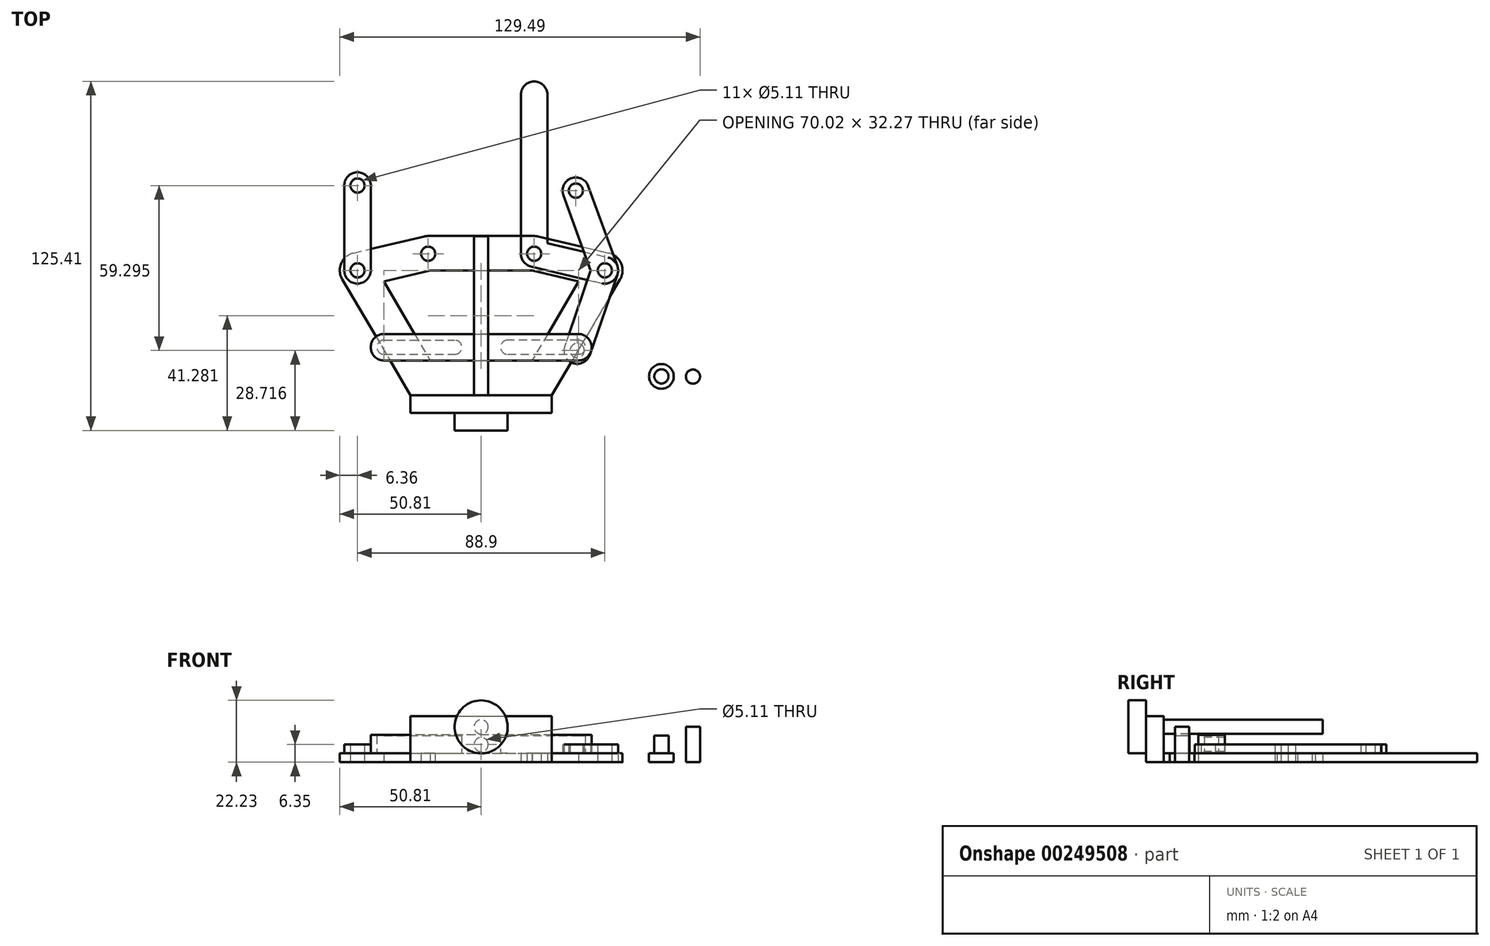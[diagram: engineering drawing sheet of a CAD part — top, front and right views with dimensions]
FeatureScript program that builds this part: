
annotation { "Feature Type Name" : "Feature", "Feature Type Description" : "" }
export const myFeature = defineFeature(function(context is Context, id is Id, definition is map)
    precondition{}
    {
        {
            var Q0;
            Q0=qCreatedBy(makeId("Top.planeOp"),FACE);
            var sketch = newSketch(context, id + "F0", { "sketchPlane" : qUnion([Q0])});
            skLineSegment(sketch, "E0", {"start": v(0, 0) * mm, "end": v(0, 50.8) * mm, "construction": true});
            skLineSegment(sketch, "E1", {"start": v(-44.45, 44.83) * mm, "end": v(44.45, 44.83) * mm, "construction": true});
            skLineSegment(sketch, "E2", {"start": v(-19.05, 50.8) * mm, "end": v(19.05, 50.8) * mm, "construction": true});
            skPoint(sketch, "E3", {"position": v(0, 44.83) * mm});
            skCircle(sketch, "E4", {"center": v(-19.05, 50.8) * mm, "radius": 2.55 * mm});
            skCircle(sketch, "E5", {"center": v(19.05, 50.8) * mm, "radius": 2.55 * mm});
            skCircle(sketch, "E6", {"center": v(44.45, 44.83) * mm, "radius": 2.55 * mm});
            skCircle(sketch, "E7", {"center": v(-44.45, 44.83) * mm, "radius": 2.55 * mm});
            skArc(sketch, "E8.0", {"start": v(20.5, 57) * mm, "mid": v(19.78, 57.12) * mm, "end": v(19.05, 57.16) * mm});
            skArc(sketch, "E9.0", {"start": v(49.93, 41.6) * mm, "mid": v(50.3, 47.33) * mm, "end": v(45.9, 51.02) * mm});
            skArc(sketch, "E10.0", {"start": v(-19.05, 57.16) * mm, "mid": v(-19.78, 57.12) * mm, "end": v(-20.5, 57) * mm});
            skArc(sketch, "E11.0", {"start": v(-45.9, 51.02) * mm, "mid": v(-50.3, 47.33) * mm, "end": v(-49.93, 41.6) * mm});
            skLineSegment(sketch, "E12", {"start": v(-25.4, 0) * mm, "end": v(25.4, 0) * mm});
            skLineSegment(sketch, "E13", {"start": v(-45.9, 51.02) * mm, "end": v(-20.5, 57) * mm});
            skLineSegment(sketch, "E14", {"start": v(-49.93, 41.6) * mm, "end": v(-25.4, 0) * mm});
            skLineSegment(sketch, "E15", {"start": v(-19.05, 57.16) * mm, "end": v(19.05, 57.16) * mm});
            skLineSegment(sketch, "E16", {"start": v(20.5, 57) * mm, "end": v(45.9, 51.02) * mm});
            skLineSegment(sketch, "E17", {"start": v(49.93, 41.6) * mm, "end": v(25.4, 0) * mm});
            skPoint(sketch, "E18", {"position": v(0, 0) * mm});
            skLineSegment(sketch, "E19.0", {"start": v(-35.01, 40.8) * mm, "end": v(-18.34, 44.72) * mm});
            skLineSegment(sketch, "E19.1", {"start": v(18.34, 44.72) * mm, "end": v(35.01, 40.8) * mm});
            skLineSegment(sketch, "E19.2", {"start": v(35.01, 40.8) * mm, "end": v(18.3, 12.45) * mm});
            skLineSegment(sketch, "E19.3", {"start": v(-18.34, 44.72) * mm, "end": v(18.34, 44.72) * mm});
            skLineSegment(sketch, "E19.4", {"start": v(-18.3, 12.45) * mm, "end": v(18.3, 12.45) * mm});
            skLineSegment(sketch, "E19.5", {"start": v(-35.01, 40.8) * mm, "end": v(-18.3, 12.45) * mm});
            skSolve(sketch);
        }
        {
            var Q0;
            Q0 = qSketchRegion(id + "F0", true);
            extrude(context, id + "F1", {"entities" : qUnion([Q0]), "depth" : 3.17 * mm});
        }
        {
            var Q0;
            Q0=makeQuery(id+"F1.opExtrude","CAP_FACE",FACE,{"disambiguationData":[OSD([sQuery(id+"F0.wireOp",EDGE,"E4"),sQuery(id+"F0.wireOp",EDGE,"E5"),sQuery(id+"F0.wireOp",EDGE,"E6"),sQuery(id+"F0.wireOp",EDGE,"E7"),sQuery(id+"F0.wireOp",EDGE,"E8.0"),sQuery(id+"F0.wireOp",EDGE,"E9.0"),sQuery(id+"F0.wireOp",EDGE,"E10.0"),sQuery(id+"F0.wireOp",EDGE,"E11.0"),sQuery(id+"F0.wireOp",EDGE,"E12"),sQuery(id+"F0.wireOp",EDGE,"E13"),sQuery(id+"F0.wireOp",EDGE,"E14"),sQuery(id+"F0.wireOp",EDGE,"E15"),sQuery(id+"F0.wireOp",EDGE,"E16"),sQuery(id+"F0.wireOp",EDGE,"E17"),sQuery(id+"F0.wireOp",EDGE,"E19.0"),sQuery(id+"F0.wireOp",EDGE,"E19.1"),sQuery(id+"F0.wireOp",EDGE,"E19.2"),sQuery(id+"F0.wireOp",EDGE,"E19.3"),sQuery(id+"F0.wireOp",EDGE,"E19.4"),sQuery(id+"F0.wireOp",EDGE,"E19.5")])],"isStart":false});
            var sketch = newSketch(context, id + "F2", { "sketchPlane" : qUnion([Q0])});
            skCircle(sketch, "E20.0", {"center": v(-44.45, 44.83) * mm, "radius": 2.55 * mm});
            skCircle(sketch, "E21", {"center": v(-44.45, 44.83) * mm, "radius": 4.76 * mm});
            skLineSegment(sketch, "E22", {"start": v(-44.45, 44.83) * mm, "end": v(-44.45, 75.31) * mm, "construction": true});
            skCircle(sketch, "E23", {"center": v(-44.45, 75.31) * mm, "radius": 4.76 * mm});
            skCircle(sketch, "E24", {"center": v(-44.45, 75.31) * mm, "radius": 2.55 * mm});
            skLineSegment(sketch, "E25", {"start": v(-49.21, 75.31) * mm, "end": v(-49.21, 44.83) * mm});
            skLineSegment(sketch, "E26", {"start": v(-39.69, 75.31) * mm, "end": v(-39.69, 44.83) * mm});
            skSolve(sketch);
        }
        {
            var Q0;
            Q0 = qSketchRegion(id + "F2", true);
            extrude(context, id + "F3", {"entities" : qUnion([Q0]), "depth" : 3.17 * mm});
        }
        {
            var Q0;
            Q0=makeQuery(id+"F2.imprint","IMPRINT",FACE,{"disambiguationData":[TD([[makeQuery(id+"F2.imprint","IMPRINT",EDGE,{"derivedFrom":makeQuery(id+"F1.opExtrude","CAP_EDGE",EDGE,{"disambiguationData":[OSD([sQuery(id+"F0.wireOp",EDGE,"E4")])],"isStart":false})}),-1.0]])]});
            var sketch = newSketch(context, id + "F4", { "sketchPlane" : qUnion([Q0])});
            skLineSegment(sketch, "E27.bottom", {"start": v(34.93, 21.97) * mm, "end": v(-34.93, 21.97) * mm});
            skLineSegment(sketch, "E27.top", {"start": v(34.93, 12.45) * mm, "end": v(-34.93, 12.45) * mm});
            skLineSegment(sketch, "E27.left", {"start": v(34.93, 21.97) * mm, "end": v(34.93, 19.76) * mm});
            skLineSegment(sketch, "E27.right", {"start": v(-34.93, 21.97) * mm, "end": v(-34.93, 19.76) * mm});
            skPoint(sketch, "E27.middle", {"position": v(0, 17.2) * mm});
            skArc(sketch, "E28", {"start": v(34.93, 12.45) * mm, "mid": v(39.69, 17.2) * mm, "end": v(34.93, 21.97) * mm});
            skArc(sketch, "E29", {"start": v(-34.93, 21.97) * mm, "mid": v(-39.69, 17.2) * mm, "end": v(-34.93, 12.45) * mm});
            skCircle(sketch, "E30.0", {"center": v(-44.45, 44.83) * mm, "radius": 2.55 * mm, "construction": true});
            skPoint(sketch, "E31.0", {"position": v(-18.3, 12.45) * mm});
            skPoint(sketch, "E32.0", {"position": v(-25.4, 0) * mm});
            skPoint(sketch, "E33.0", {"position": v(18.3, 12.45) * mm});
            skPoint(sketch, "E34.0", {"position": v(25.4, 0) * mm});
            skLineSegment(sketch, "E35", {"start": v(-18.3, 12.45) * mm, "end": v(-25.4, 0) * mm, "construction": true});
            skLineSegment(sketch, "E36", {"start": v(18.3, 12.45) * mm, "end": v(25.4, 0) * mm, "construction": true});
            skLineSegment(sketch, "E37.0", {"start": v(-18.3, 12.45) * mm, "end": v(18.3, 12.45) * mm, "construction": true});
            skArc(sketch, "E38", {"start": v(34.93, 14.66) * mm, "mid": v(37.48, 17.2) * mm, "end": v(34.93, 19.76) * mm});
            skArc(sketch, "E39", {"start": v(-34.93, 19.76) * mm, "mid": v(-37.48, 17.2) * mm, "end": v(-34.93, 14.66) * mm});
            skArc(sketch, "E40", {"start": v(-9.53, 14.66) * mm, "mid": v(-6.97, 17.2) * mm, "end": v(-9.53, 19.76) * mm});
            skArc(sketch, "E41", {"start": v(9.53, 19.76) * mm, "mid": v(6.97, 17.2) * mm, "end": v(9.53, 14.66) * mm});
            skLineSegment(sketch, "E42", {"start": v(-34.93, 19.76) * mm, "end": v(-9.53, 19.76) * mm});
            skLineSegment(sketch, "E43", {"start": v(-34.93, 14.66) * mm, "end": v(-9.53, 14.66) * mm});
            skLineSegment(sketch, "E44", {"start": v(9.53, 14.66) * mm, "end": v(34.93, 14.66) * mm});
            skLineSegment(sketch, "E45", {"start": v(34.93, 19.76) * mm, "end": v(9.53, 19.76) * mm});
            skLineSegment(sketch, "E46", {"start": v(-34.93, 17.2) * mm, "end": v(-9.53, 17.2) * mm, "construction": true});
            skLineSegment(sketch, "E47", {"start": v(9.53, 17.2) * mm, "end": v(34.93, 17.2) * mm, "construction": true});
            skLineSegment(sketch, "E48.trimOffspring", {"start": v(34.93, 14.66) * mm, "end": v(34.93, 12.45) * mm});
            skLineSegment(sketch, "E49.trimOffspring", {"start": v(-34.93, 14.66) * mm, "end": v(-34.93, 12.45) * mm});
            skSolve(sketch);
        }
        {
            var Q0;
            Q0 = qSketchRegion(id + "F4", true);
            extrude(context, id + "F5", {"entities" : qUnion([Q0]), "depth" : 6.35 * mm});
        }
        {
            var Q0;
            Q0=makeQuery(id+"F2.imprint","IMPRINT",FACE,{"disambiguationData":[TD([[makeQuery(id+"F2.imprint","IMPRINT",EDGE,{"derivedFrom":makeQuery(id+"F1.opExtrude","CAP_EDGE",EDGE,{"disambiguationData":[OSD([sQuery(id+"F0.wireOp",EDGE,"E4")])],"isStart":false})}),-1.0]])]});
            var sketch = newSketch(context, id + "F6", { "sketchPlane" : qUnion([Q0])});
            skCircle(sketch, "E50.0", {"center": v(44.45, 44.83) * mm, "radius": 2.55 * mm});
            skArc(sketch, "E51", {"start": v(48.95, 43.28) * mm, "mid": v(49.21, 44.87) * mm, "end": v(48.93, 46.46) * mm});
            skArc(sketch, "E52", {"start": v(38.5, 75.1) * mm, "mid": v(32.4, 77.95) * mm, "end": v(29.55, 71.84) * mm});
            skLineSegment(sketch, "E53", {"start": v(34.03, 73.47) * mm, "end": v(44.45, 44.83) * mm, "construction": true});
            skLineSegment(sketch, "E54", {"start": v(38.5, 75.1) * mm, "end": v(48.93, 46.46) * mm});
            skLineSegment(sketch, "E55", {"start": v(29.55, 71.84) * mm, "end": v(39.4, 44.79) * mm});
            skCircle(sketch, "E56", {"center": v(34.03, 73.47) * mm, "radius": 2.55 * mm});
            skCircle(sketch, "E57.0", {"center": v(34.51, 16.02) * mm, "radius": 2.55 * mm});
            skCircle(sketch, "E58", {"center": v(34.51, 16.02) * mm, "radius": 4.76 * mm});
            skLineSegment(sketch, "E59", {"start": v(39.4, 44.79) * mm, "end": v(30.01, 17.57) * mm});
            skLineSegment(sketch, "E60", {"start": v(48.95, 43.28) * mm, "end": v(39.02, 14.46) * mm});
            skSolve(sketch);
        }
        {
            var Q0;
            Q0 = qSketchRegion(id + "F6", true);
            extrude(context, id + "F7", {"entities" : qUnion([Q0]), "depth" : 3.17 * mm});
        }
        {
            var Q0;
            Q0=qCreatedBy(makeId("Top.planeOp"),FACE);
            var sketch = newSketch(context, id + "F8", { "sketchPlane" : qUnion([Q0])});
            skCircle(sketch, "E61", {"center": v(64.8, 6.73) * mm, "radius": 4.45 * mm});
            skSolve(sketch);
        }
        {
            var Q0;
            Q0 = qSketchRegion(id + "F8", true);
            extrude(context, id + "F9", {"entities" : qUnion([Q0]), "depth" : 3.17 * mm});
        }
        {
            var Q0;
            Q0=makeQuery(id+"F9.opExtrude","CAP_FACE",FACE,{"disambiguationData":[OSD([sQuery(id+"F8.wireOp",EDGE,"E61")])],"isStart":false});
            var sketch = newSketch(context, id + "F10", { "sketchPlane" : qUnion([Q0])});
            skCircle(sketch, "E62", {"center": v(64.8, 6.73) * mm, "radius": 2.55 * mm});
            skSolve(sketch);
        }
        {
            var Q0;
            Q0 = qSketchRegion(id + "F10", true);
            extrude(context, id + "F11", {"entities" : qUnion([Q0]), "operationType" : NewBodyOperationType.ADD, "depth" : 6.35 * mm});
        }
        {
            var Q0;
            Q0=qCreatedBy(makeId("Top.planeOp"),FACE);
            var sketch = newSketch(context, id + "F12", { "sketchPlane" : qUnion([Q0])});
            skCircle(sketch, "E63.0", {"center": v(19.05, 50.8) * mm, "radius": 2.55 * mm});
            skCircle(sketch, "E64.0", {"center": v(44.45, 44.83) * mm, "radius": 2.55 * mm});
            skCircle(sketch, "E65", {"center": v(19.05, 50.8) * mm, "radius": 4.76 * mm});
            skCircle(sketch, "E66", {"center": v(44.45, 44.83) * mm, "radius": 4.76 * mm});
            skLineSegment(sketch, "E67", {"start": v(20.14, 55.44) * mm, "end": v(45.54, 49.47) * mm});
            skLineSegment(sketch, "E68", {"start": v(17.96, 46.16) * mm, "end": v(43.36, 40.2) * mm});
            skCircle(sketch, "E69", {"center": v(19.05, 107.95) * mm, "radius": 4.76 * mm});
            skLineSegment(sketch, "E70", {"start": v(14.29, 107.95) * mm, "end": v(14.29, 50.8) * mm});
            skLineSegment(sketch, "E71", {"start": v(23.81, 50.8) * mm, "end": v(23.81, 107.95) * mm});
            skSolve(sketch);
        }
        {
            var Q0;
            Q0 = qSketchRegion(id + "F12", true);
            extrude(context, id + "F13", {"entities" : qUnion([Q0]), "depth" : 3.17 * mm});
        }
        {
            var Q0;
            Q0=qCreatedBy(makeId("Top.planeOp"),FACE);
            var sketch = newSketch(context, id + "F14", { "sketchPlane" : qUnion([Q0])});
            skCircle(sketch, "E72", {"center": v(76.12, 6.64) * mm, "radius": 2.55 * mm});
            skSolve(sketch);
        }
        {
            var Q0;
            Q0 = qSketchRegion(id + "F14", true);
            extrude(context, id + "F15", {"entities" : qUnion([Q0]), "depth" : 12.7 * mm});
        }
        {
            var Q0;
            Q0=makeQuery(id+"F5.opExtrude","CAP_FACE",FACE,{"disambiguationData":[OSD([sQuery(id+"F4.wireOp",EDGE,"E27.bottom"),sQuery(id+"F4.wireOp",EDGE,"E27.top"),sQuery(id+"F4.wireOp",EDGE,"E28"),sQuery(id+"F4.wireOp",EDGE,"E29"),sQuery(id+"F4.wireOp",EDGE,"E38"),sQuery(id+"F4.wireOp",EDGE,"E39"),sQuery(id+"F4.wireOp",EDGE,"E40"),sQuery(id+"F4.wireOp",EDGE,"E41"),sQuery(id+"F4.wireOp",EDGE,"E42"),sQuery(id+"F4.wireOp",EDGE,"E43"),sQuery(id+"F4.wireOp",EDGE,"E44"),sQuery(id+"F4.wireOp",EDGE,"E45")])],"isStart":false});
            var sketch = newSketch(context, id + "F16", { "sketchPlane" : qUnion([Q0])});
            skLineSegment(sketch, "E73.0", {"start": v(34.93, 21.97) * mm, "end": v(34.93, 21.97) * mm});
            skLineSegment(sketch, "E74.0", {"start": v(34.93, 21.97) * mm, "end": v(-34.93, 21.97) * mm});
            skArc(sketch, "E75.0", {"start": v(34.93, 12.45) * mm, "mid": v(39.69, 17.2) * mm, "end": v(34.93, 21.97) * mm});
            skLineSegment(sketch, "E76.0", {"start": v(34.93, 12.45) * mm, "end": v(-34.93, 12.45) * mm});
            skArc(sketch, "E77.0", {"start": v(-34.93, 21.97) * mm, "mid": v(-39.69, 17.2) * mm, "end": v(-34.93, 12.45) * mm});
            skSolve(sketch);
        }
        {
            var Q0;
            Q0 = qSketchRegion(id + "F16", true);
            extrude(context, id + "F17", {"entities" : qUnion([Q0]), "operationType" : NewBodyOperationType.ADD, "depth" : 0.25 * mm});
        }
        {
            var Q0;
            Q0=makeQuery(id+"F17.boolean.opBoolean","MERGE",FACE,{"derivedFrom":[makeQuery(id+"F5.opExtrude","SWEPT_FACE",FACE,{"disambiguationData":[OSD([sQuery(id+"F4.wireOp",EDGE,"E27.top")])]}),makeQuery(id+"F17.opExtrude","SWEPT_FACE",FACE,{"disambiguationData":[OSD([sQuery(id+"F16.wireOp",EDGE,"890eed87-c472-4494-b1f9-d9110c023a10.0")])]})]});
            var sketch = newSketch(context, id + "F18", { "sketchPlane" : qUnion([Q0])});
            skCircle(sketch, "E78", {"center": v(0, 6.35) * mm, "radius": 2.55 * mm});
            skSolve(sketch);
        }
        {
            var Q0;
            Q0 = qSketchRegion(id + "F18", true);
            var Q1;
            Q1=makeQuery(id+"F17.boolean.opBoolean","MERGE",FACE,{"derivedFrom":[makeQuery(id+"F5.opExtrude","SWEPT_FACE",FACE,{"disambiguationData":[OSD([sQuery(id+"F4.wireOp",EDGE,"E27.bottom")])]}),makeQuery(id+"F17.opExtrude","SWEPT_FACE",FACE,{"disambiguationData":[OSD([sQuery(id+"F16.wireOp",EDGE,"dfc19453-a133-409c-81e9-14027c819ca3.0")])]})]});
            extrude(context, id + "F19", {"entities" : qUnion([Q0]), "operationType" : NewBodyOperationType.REMOVE, "endBound" : BoundingType.UP_TO_SURFACE, "oppositeDirection" : true, "endBoundEntityFace" : qUnion([Q1]), "depth" : 25.4 * mm});
        }
        {
            var Q0;
            Q0=makeQuery(id+"F1.opExtrude","SWEPT_FACE",FACE,{"disambiguationData":[OSD([sQuery(id+"F0.wireOp",EDGE,"E12")])]});
            var sketch = newSketch(context, id + "F20", { "sketchPlane" : qUnion([Q0])});
            skLineSegment(sketch, "E79.bottom", {"start": v(-25.4, 0) * mm, "end": v(25.4, 0) * mm});
            skLineSegment(sketch, "E79.top", {"start": v(-25.4, 16.5) * mm, "end": v(25.4, 16.5) * mm});
            skLineSegment(sketch, "E79.left", {"start": v(-25.4, 0) * mm, "end": v(-25.4, 16.5) * mm});
            skLineSegment(sketch, "E79.right", {"start": v(25.4, 0) * mm, "end": v(25.4, 16.5) * mm});
            skCircle(sketch, "E80", {"center": v(0, 12.7) * mm, "radius": 2.55 * mm});
            skSolve(sketch);
        }
        {
            var Q0;
            Q0 = qSketchRegion(id + "F20", true);
            extrude(context, id + "F21", {"entities" : qUnion([Q0]), "operationType" : NewBodyOperationType.ADD, "depth" : 6.35 * mm});
        }
        {
            var Q0;
            Q0=makeQuery(id+"F21.opExtrude","CAP_FACE",FACE,{"disambiguationData":[OSD([sQuery(id+"F20.wireOp",EDGE,"E79.bottom"),sQuery(id+"F20.wireOp",EDGE,"E79.top"),sQuery(id+"F20.wireOp",EDGE,"E79.left"),sQuery(id+"F20.wireOp",EDGE,"E79.right"),sQuery(id+"F20.wireOp",EDGE,"E80")])],"isStart":false});
            var sketch = newSketch(context, id + "F22", { "sketchPlane" : qUnion([Q0])});
            skCircle(sketch, "E81.0", {"center": v(0, 12.7) * mm, "radius": 2.55 * mm});
            skSolve(sketch);
        }
        {
            var Q0;
            Q0 = qSketchRegion(id + "F22", true);
            extrude(context, id + "F23", {"entities" : qUnion([Q0]), "oppositeDirection" : true, "depth" : 63.5 * mm});
        }
        {
            var Q0;
            Q0=makeQuery(id+"F23.opExtrude","CAP_FACE",FACE,{"disambiguationData":[OSD([sQuery(id+"F22.wireOp",EDGE,"E81.0")])],"isStart":true});
            var sketch = newSketch(context, id + "F24", { "sketchPlane" : qUnion([Q0])});
            skCircle(sketch, "E82.0", {"center": v(0, 12.7) * mm, "radius": 2.55 * mm, "construction": true});
            skCircle(sketch, "E83", {"center": v(0, 12.7) * mm, "radius": 9.53 * mm});
            skSolve(sketch);
        }
        {
            var Q0;
            Q0 = qSketchRegion(id + "F24", true);
            extrude(context, id + "F25", {"entities" : qUnion([Q0]), "operationType" : NewBodyOperationType.ADD, "depth" : 6.35 * mm});
        }
    });
